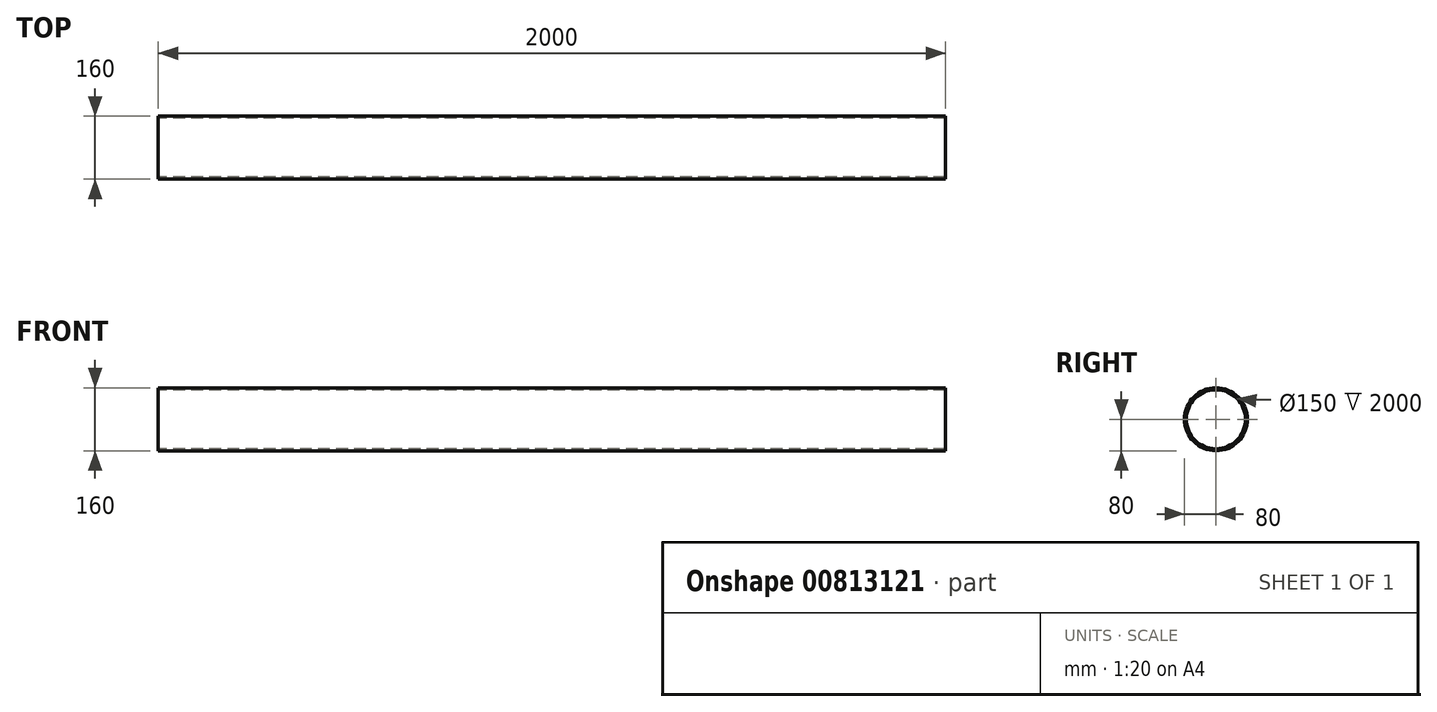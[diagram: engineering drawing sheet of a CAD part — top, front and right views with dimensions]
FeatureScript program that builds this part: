
annotation { "Feature Type Name" : "Feature", "Feature Type Description" : "" }
export const myFeature = defineFeature(function(context is Context, id is Id, definition is map)
    precondition{}
    {
        {
            var Q0;
            Q0=qCreatedBy(makeId("Right.planeOp"),FACE);
            var sketch = newSketch(context, id + "F0", { "sketchPlane" : qUnion([Q0])});
            skCircle(sketch, "E0", {"center": v(0, 0) * mm, "radius": 75 * mm});
            skCircle(sketch, "E1", {"center": v(0, 0) * mm, "radius": 80 * mm});
            skSolve(sketch);
        }
        {
            var Q0;
            Q0=makeQuery(id+"F0.imprint","IMPRINT",FACE,{"disambiguationData":[TD([[makeQuery(id+"F0.imprint","IMPRINT",EDGE,{"derivedFrom":sQuery(id+"F0.wireOp",EDGE,"E0")}),-1.0]])]});
            extrude(context, id + "F1", {"entities" : qUnion([Q0]), "endBound" : BoundingType.SYMMETRIC, "depth" : 2000 * mm, "offsetDistance" : 25 * mm});
        }
    });
